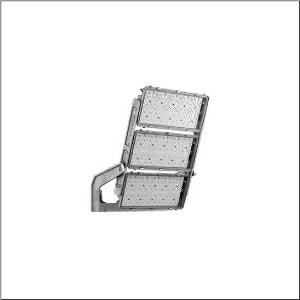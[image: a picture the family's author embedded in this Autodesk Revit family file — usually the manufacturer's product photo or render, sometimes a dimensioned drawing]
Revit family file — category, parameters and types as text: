
# Revit family: floodlight_fl_11_maxi_pro_remote___pl52_5xa779426d01aa_14f9
name_source: partatom
category: Lighting Fixtures
units: mm (PartAtom-declared; Revit-internal decimal feet)

## family parameters
Cut with Voids When Loaded = No
Host = Face
Light Source = No
Part Type = Normal
Room Calculation Point = No
Round Connector Dimension = Use Diameter
Shared = No

## types (1)
- --- (1 x LED, 169140 lm, 1387.6 W, 4000K)
    Apparent Load = 1388 VA
    CIE Flux Codes = 24 55 98 100 100
    Color Rendering = 70
    Color Temperature = 4000K
    Default Elevation = 1800 mm
    Description = Floodlight FL 11  maxi  pro Remote floodlight; light control with lens of PMMA; cover panel of toughened safety glass, transparent; light distribution: PL52, asymmetric direct distribution, LEDcolour temperature: 4000K, rated luminous flux: 169.140lm, colour rendering: CRI > 70, light colour: 740; luminous efficacy: 122lm/W; brightness control: DALI 2 (1 DALI address); with terminal, 8-pole, max. 2.5mm², mains connection: 220..240V/380..400V AC, 50/60Hz, surge voltage resistance: line to ground: 10kV, ECG replaceable separately, LED unit replaceable without ESD environment, dustproof LED module, dimming range 10..100%, no afterglow with DALI off / DMX off command; 1388W floodlight with 3x LED unit of diecast aluminium, coated grey; length: 713mm / width: 651mm / height: 338mm; mounting bracket, of diecast aluminium, uncoated, natural, equipment: Power, protection rating (complete): IP66; insulation class (complete): insulation class I (protective earthing); certification: CE, ENEC, VDE; ball protection: ball impact resistance with accessories, impact resistance: IK07; rated ambient temperature 10°C, only for outdoor installations, permissible operating ambient temperature: -40..+30°C, permissible storage temperature: -40..+85°Cpackaging unit: 1 piece

Light Distribution: PL52
    Height = 320 mm
    Lamp = 1 x LED
    Lamp Light Flux = 169140 lm
    Lamp Power = 1387.6 W
    Lamp count = 1
    Length = 1002 mm
    Luminous efficacy = 122 lm/W
    Manufacturer = Siteco
    ModVariant = No
    Model = 5XA779426D01AA
    Mounting Place = Ceiling
    Mounting Type = Surface mounted
    Number of Poles = 1
    OnlyDefault = Yes
    Power Factor = 1
    Product Name = Floodlight FL 11 maxi pro Remote | PL52
    Product group = floodlight | ceiling mounted
    ProductGroupID = 301
    Protection Class = Protection class I
    Protection Degree = IP 66
    RLX_Detail_Level = 1
    RLX_Emergency_Light_Flux = 0 lm
    RLX_Emergency_Type = 0
    RLX_Emergency_Type_DB = No
    RlxData = <blob elided: 52581 chars, md5=858374e3>
    Socket = socket
    Standby Power = 0 W
    System Light Flux = 169140 lm
    System Power = 1388 W
    Type Comments = factory setting: luminous flux: 100 % | dim-lin: 254 | 955 mA
    Type Image = l_1349141.jpg
    URL = http://relux.com
    VarID = @adj_097902
    Voltage = 0 V
    Weight = 0.00 kg
    Width = 655 mm

## geometry (parser evidence)
native form markers: Blend x4, Sweep x12
no freeform markers — native parametric forms only
